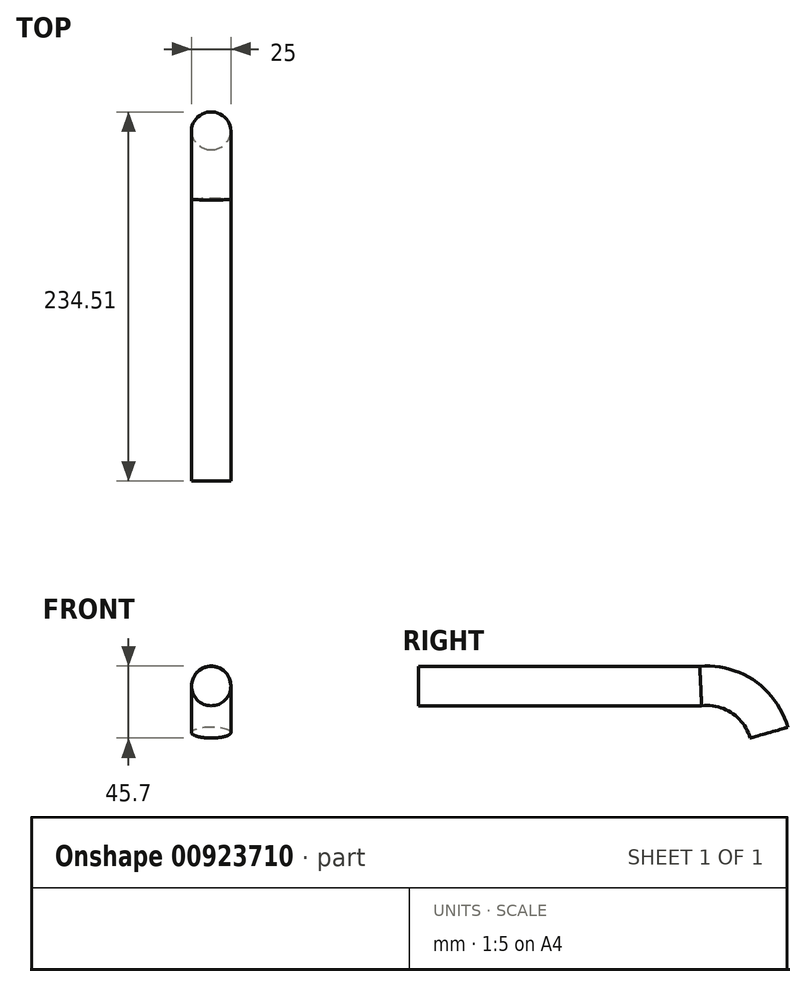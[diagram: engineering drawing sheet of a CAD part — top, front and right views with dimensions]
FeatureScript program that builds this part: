
annotation { "Feature Type Name" : "Feature", "Feature Type Description" : "" }
export const myFeature = defineFeature(function(context is Context, id is Id, definition is map)
    precondition{}
    {
        {
            var Q0;
            Q0=qCreatedBy(makeId("Front.planeOp"),FACE);
            var sketch = newSketch(context, id + "F0", { "sketchPlane" : qUnion([Q0])});
            skCircle(sketch, "E0", {"center": v(0, 0) * mm, "radius": 12.5 * mm});
            skSolve(sketch);
        }
        {
            var Q0;
            Q0=qCreatedBy(makeId("Right.planeOp"),FACE);
            var sketch = newSketch(context, id + "F1", { "sketchPlane" : qUnion([Q0])});
            skLineSegment(sketch, "E1", {"start": v(0, 0) * mm, "end": v(179.12, 0) * mm});
            skArc(sketch, "E2", {"start": v(222.49, -29.6) * mm, "mid": v(206.17, -6.94) * mm, "end": v(179.12, 0) * mm});
            skSolve(sketch);
        }
        {
            var Q0;
            Q0=makeQuery(id+"F0.imprint","IMPRINT",FACE,{"disambiguationData":[TD([[makeQuery(id+"F0.imprint","IMPRINT",EDGE,{"derivedFrom":sQuery(id+"F0.wireOp",EDGE,"E0")}),1.0]])]});
            var Q1;
            Q1=sQuery(id+"F1.wireOp",EDGE,"E1");
            var Q2;
            Q2=sQuery(id+"F1.wireOp",EDGE,"E2");
            sweep(context, id + "F2", {"profiles" : qUnion([Q0]), "path" : qUnion([Q1, Q2])});
        }
    });
